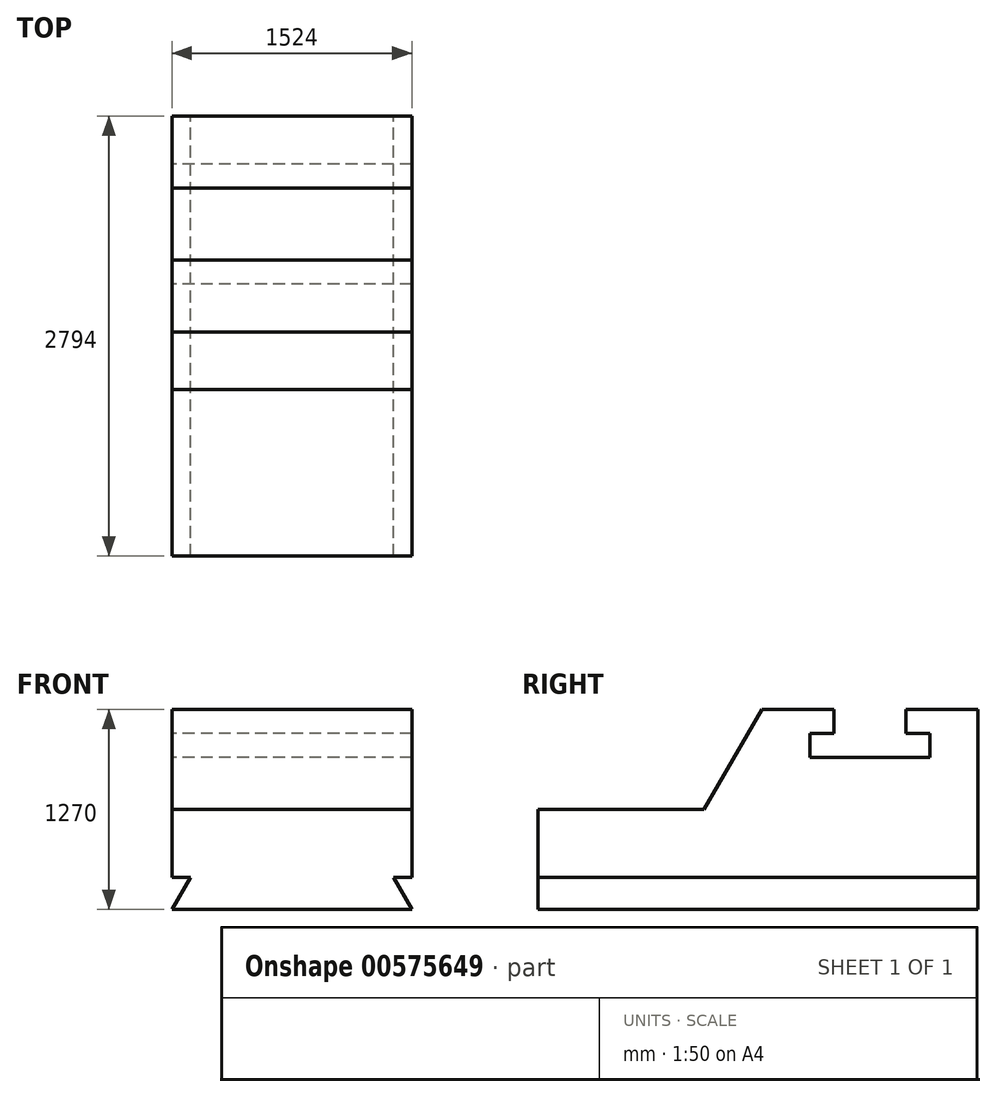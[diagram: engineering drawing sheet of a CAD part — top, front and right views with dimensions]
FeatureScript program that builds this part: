
annotation { "Feature Type Name" : "Feature", "Feature Type Description" : "" }
export const myFeature = defineFeature(function(context is Context, id is Id, definition is map)
    precondition{}
    {
        {
            var Q0;
            Q0=qCreatedBy(makeId("Right.planeOp"),FACE);
            var sketch = newSketch(context, id + "F0", { "sketchPlane" : qUnion([Q0])});
            skLineSegment(sketch, "E0", {"start": v(0, 0) * mm, "end": v(2794, 0) * mm});
            skLineSegment(sketch, "E1", {"start": v(2794, 0) * mm, "end": v(2794, 1270) * mm});
            skLineSegment(sketch, "E2", {"start": v(2794, 1270) * mm, "end": v(2336.8, 1270) * mm});
            skLineSegment(sketch, "E3", {"start": v(2336.8, 1270) * mm, "end": v(2336.8, 1117.6) * mm});
            skLineSegment(sketch, "E4", {"start": v(2336.8, 1117.6) * mm, "end": v(2489.2, 1117.6) * mm});
            skLineSegment(sketch, "E5", {"start": v(2489.2, 1117.6) * mm, "end": v(2489.2, 965.2) * mm});
            skLineSegment(sketch, "E6", {"start": v(2489.2, 965.2) * mm, "end": v(1727.2, 965.2) * mm});
            skLineSegment(sketch, "E7", {"start": v(1727.2, 965.2) * mm, "end": v(1727.2, 1117.6) * mm});
            skLineSegment(sketch, "E8", {"start": v(1727.2, 1117.6) * mm, "end": v(1879.6, 1117.6) * mm});
            skLineSegment(sketch, "E9", {"start": v(1879.6, 1117.6) * mm, "end": v(1879.6, 1270) * mm});
            skLineSegment(sketch, "E10", {"start": v(1879.6, 1270) * mm, "end": v(1422.4, 1270) * mm});
            skLineSegment(sketch, "E11", {"start": v(0, 0) * mm, "end": v(0, 635) * mm});
            skLineSegment(sketch, "E12", {"start": v(0, 635) * mm, "end": v(1055.78, 635) * mm});
            skLineSegment(sketch, "E13", {"start": v(1055.78, 635) * mm, "end": v(1422.4, 1270) * mm});
            skLineSegment(sketch, "E14", {"start": v(0, 0) * mm, "end": v(0, 203.2) * mm});
            skLineSegment(sketch, "E15", {"start": v(0, 203.2) * mm, "end": v(2794, 203.2) * mm});
            skSolve(sketch);
        }
        {
            var Q0;
            {var subQ0=sQuery(id+"F0.wireOp",EDGE,"E2");Q0=makeQuery(id+"F0.imprint","IMPRINT",FACE,{"disambiguationData":[TD([[makeQuery(id+"F0.imprint","IMPRINT",EDGE,{"derivedFrom":subQ0}),1.0]])]});}
            extrude(context, id + "F1", {"entities" : qUnion([Q0]), "depth" : 1524 * mm, "offsetDistance" : 25.4 * mm});
        }
        {
            var Q0;
            Q0=qCreatedBy(makeId("Front.planeOp"),FACE);
            var sketch = newSketch(context, id + "F2", { "sketchPlane" : qUnion([Q0])});
            skLineSegment(sketch, "E16", {"start": v(0, 0) * mm, "end": v(1524, 0) * mm});
            skLineSegment(sketch, "E17", {"start": v(1524, 0) * mm, "end": v(1524, 203.2) * mm});
            skLineSegment(sketch, "E18", {"start": v(0, 0) * mm, "end": v(0, 203.2) * mm});
            skLineSegment(sketch, "E19", {"start": v(0, 203.2) * mm, "end": v(1524, 203.2) * mm});
            skSolve(sketch);
        }
        {
            var Q0;
            Q0=makeQuery(id+"F2.imprint","IMPRINT",FACE,{"disambiguationData":[TD([[makeQuery(id+"F2.imprint","IMPRINT",EDGE,{"derivedFrom":sQuery(id+"F2.wireOp",EDGE,"E16")}),1.0]])]});
            extrude(context, id + "F3", {"entities" : qUnion([Q0]), "operationType" : NewBodyOperationType.ADD, "oppositeDirection" : true, "depth" : 2794 * mm, "offsetDistance" : 25.4 * mm});
        }
        {
            var Q0;
            Q0=makeQuery(id+"F3.boolean.opBoolean","MERGE",FACE,{"derivedFrom":[makeQuery(id+"F1.opExtrude","SWEPT_FACE",FACE,{"disambiguationData":[OSD([sQuery(id+"F0.wireOp",EDGE,"E1")])]}),makeQuery(id+"F3.opExtrude","CAP_FACE",FACE,{"disambiguationData":[OSD([sQuery(id+"F2.wireOp",EDGE,"E16"),sQuery(id+"F2.wireOp",EDGE,"E17"),sQuery(id+"F2.wireOp",EDGE,"E18"),sQuery(id+"F2.wireOp",EDGE,"E19")])],"isStart":false})]});
            var sketch = newSketch(context, id + "F4", { "sketchPlane" : qUnion([Q0])});
            skLineSegment(sketch, "E20", {"start": v(-1524, 0) * mm, "end": v(-1406.68, 203.2) * mm});
            skLineSegment(sketch, "E21", {"start": v(-1406.68, 203.2) * mm, "end": v(-1524, 203.2) * mm});
            skLineSegment(sketch, "E22", {"start": v(0, 0) * mm, "end": v(-117.32, 203.2) * mm});
            skLineSegment(sketch, "E23", {"start": v(-117.32, 203.2) * mm, "end": v(0, 203.2) * mm});
            skSolve(sketch);
        }
        {
            var Q0;
            {var subQ0=sQuery(id+"F4.wireOp",EDGE,"E20");Q0=makeQuery(id+"F4.imprint","IMPRINT",FACE,{"disambiguationData":[TD([[makeQuery(id+"F4.imprint","IMPRINT",EDGE,{"derivedFrom":subQ0}),1.0]])]});}
            var Q1;
            {var subQ0=sQuery(id+"F4.wireOp",EDGE,"E22");Q1=makeQuery(id+"F4.imprint","IMPRINT",FACE,{"disambiguationData":[TD([[makeQuery(id+"F4.imprint","IMPRINT",EDGE,{"derivedFrom":subQ0}),-1.0]])]});}
            extrude(context, id + "F5", {"entities" : qUnion([Q0, Q1]), "operationType" : NewBodyOperationType.REMOVE, "oppositeDirection" : true, "depth" : 2794 * mm, "offsetDistance" : 25.4 * mm});
        }
    });
